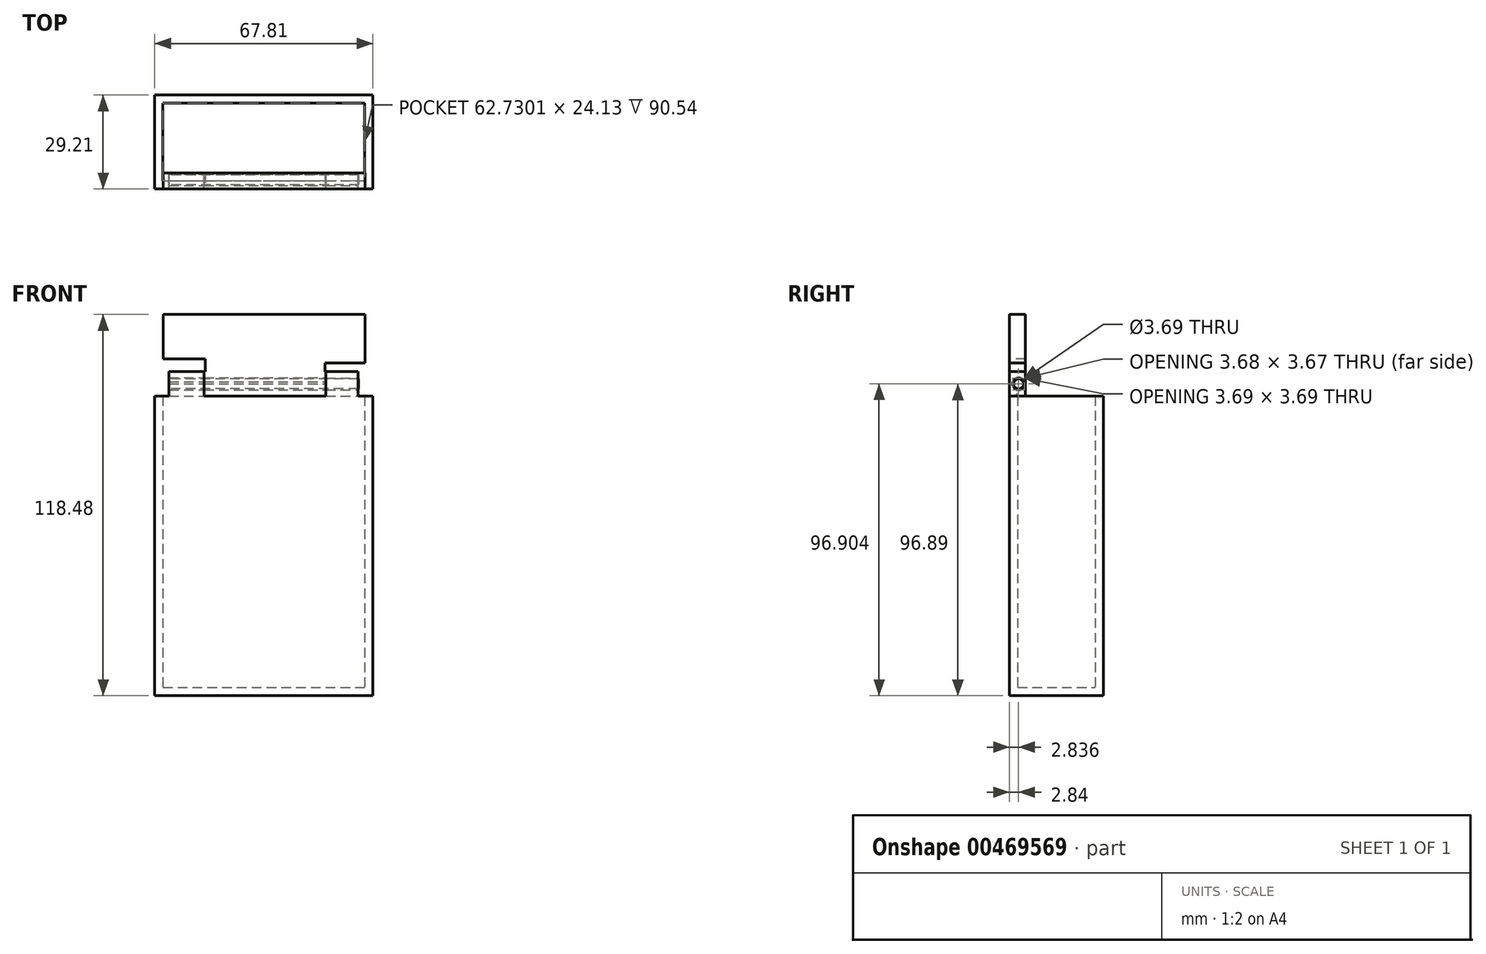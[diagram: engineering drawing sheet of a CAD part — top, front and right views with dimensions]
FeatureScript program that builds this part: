
annotation { "Feature Type Name" : "Feature", "Feature Type Description" : "" }
export const myFeature = defineFeature(function(context is Context, id is Id, definition is map)
    precondition{}
    {
        {
            var Q0;
            Q0=qCreatedBy(makeId("Top.planeOp"),FACE);
            var sketch = newSketch(context, id + "F0", { "sketchPlane" : qUnion([Q0])});
            skLineSegment(sketch, "E0.bottom", {"start": v(0, 0) * mm, "end": v(67.81, 0) * mm});
            skLineSegment(sketch, "E0.top", {"start": v(0, 29.21) * mm, "end": v(67.81, 29.21) * mm});
            skLineSegment(sketch, "E0.left", {"start": v(0, 0) * mm, "end": v(0, 29.21) * mm});
            skLineSegment(sketch, "E0.right", {"start": v(67.81, 0) * mm, "end": v(67.81, 29.21) * mm});
            skSolve(sketch);
        }
        {
            var Q0;
            Q0 = qSketchRegion(id + "F0", true);
            extrude(context, id + "F1", {"entities" : qUnion([Q0]), "depth" : 93.08 * mm});
        }
        {
            var Q0;
            Q0=makeQuery(id+"F1.opExtrude","CAP_FACE",FACE,{"disambiguationData":[OSD([sQuery(id+"F0.wireOp",EDGE,"E0.bottom"),sQuery(id+"F0.wireOp",EDGE,"E0.top"),sQuery(id+"F0.wireOp",EDGE,"E0.left"),sQuery(id+"F0.wireOp",EDGE,"E0.right")])],"isStart":false});
            shell(context, id + "F2", {"entities" : qUnion([Q0]), "thickness" : 2.54 * mm});
        }
        {
            var Q0;
            Q0=makeQuery(id+"F1.opExtrude","CAP_FACE",FACE,{"disambiguationData":[OSD([sQuery(id+"F0.wireOp",EDGE,"E0.bottom"),sQuery(id+"F0.wireOp",EDGE,"E0.top"),sQuery(id+"F0.wireOp",EDGE,"E0.left"),sQuery(id+"F0.wireOp",EDGE,"E0.right")])],"isStart":false});
            var sketch = newSketch(context, id + "F3", { "sketchPlane" : qUnion([Q0])});
            skLineSegment(sketch, "E1.bottom", {"start": v(4.45, 0) * mm, "end": v(15.39, 0) * mm});
            skLineSegment(sketch, "E1.top", {"start": v(4.45, 4.96) * mm, "end": v(15.39, 4.96) * mm});
            skLineSegment(sketch, "E1.left", {"start": v(4.45, 0) * mm, "end": v(4.45, 4.96) * mm});
            skLineSegment(sketch, "E1.right", {"start": v(15.39, 0) * mm, "end": v(15.39, 4.96) * mm});
            skLineSegment(sketch, "E2.bottom", {"start": v(63.22, 0) * mm, "end": v(53.2, 0) * mm});
            skLineSegment(sketch, "E2.top", {"start": v(63.22, 4.96) * mm, "end": v(53.2, 4.96) * mm});
            skLineSegment(sketch, "E2.left", {"start": v(63.22, 0) * mm, "end": v(63.22, 4.96) * mm});
            skLineSegment(sketch, "E2.right", {"start": v(53.2, 0) * mm, "end": v(53.2, 4.96) * mm});
            skSolve(sketch);
        }
        {
            var Q0;
            Q0 = qSketchRegion(id + "F3", true);
            extrude(context, id + "F4", {"entities" : qUnion([Q0]), "operationType" : NewBodyOperationType.ADD, "depth" : 7.62 * mm});
        }
        {
            var Q0;
            {var subQ2=sQuery(id+"F0.wireOp",EDGE,"E0.bottom");var subQ3=sQuery(id+"F3.wireOp",EDGE,"E1.right");Q0=makeQuery(id+"F4.boolean.opBoolean","SPLIT",FACE,{"disambiguationData":[TD([makeQuery(id+"F4.opExtrude","SWEPT_FACE",FACE,{"disambiguationData":[OSD([subQ3])]})])],"derivedFrom":makeQuery(id+"F1.opExtrude","CAP_FACE",FACE,{"disambiguationData":[OSD([subQ2,sQuery(id+"F0.wireOp",EDGE,"E0.top"),sQuery(id+"F0.wireOp",EDGE,"E0.left"),sQuery(id+"F0.wireOp",EDGE,"E0.right")])],"isStart":false})});}
            var sketch = newSketch(context, id + "F5", { "sketchPlane" : qUnion([Q0])});
            skLineSegment(sketch, "E3.bottom", {"start": v(15.39, 4.96) * mm, "end": v(53.2, 4.96) * mm});
            skLineSegment(sketch, "E3.top", {"start": v(15.39, 0) * mm, "end": v(53.2, 0) * mm});
            skLineSegment(sketch, "E3.left", {"start": v(15.39, 4.96) * mm, "end": v(15.39, 0) * mm});
            skLineSegment(sketch, "E3.right", {"start": v(53.2, 4.96) * mm, "end": v(53.2, 0) * mm});
            skSolve(sketch);
        }
        {
            var Q0;
            Q0 = qSketchRegion(id + "F5", true);
            extrude(context, id + "F6", {"entities" : qUnion([Q0]), "depth" : 25.4 * mm});
        }
        {
            var Q0;
            Q0=makeQuery(id+"F6.opExtrude","SWEPT_FACE",FACE,{"disambiguationData":[OSD([sQuery(id+"F5.wireOp",EDGE,"E3.left")])]});
            var sketch = newSketch(context, id + "F7", { "sketchPlane" : qUnion([Q0])});
            skLineSegment(sketch, "E4.bottom", {"start": v(-4.96, 100.75) * mm, "end": v(0, 100.75) * mm});
            skLineSegment(sketch, "E4.top", {"start": v(-4.96, 118.48) * mm, "end": v(0, 118.48) * mm});
            skLineSegment(sketch, "E4.left", {"start": v(-4.96, 100.75) * mm, "end": v(-4.96, 118.48) * mm});
            skLineSegment(sketch, "E4.right", {"start": v(0, 100.75) * mm, "end": v(0, 118.48) * mm});
            skSolve(sketch);
        }
        {
            var Q0;
            Q0 = qSketchRegion(id + "F7", true);
            extrude(context, id + "F8", {"entities" : qUnion([Q0]), "operationType" : NewBodyOperationType.ADD, "depth" : 12.7 * mm});
        }
        {
            var Q0;
            Q0=makeQuery(id+"F6.opExtrude","SWEPT_FACE",FACE,{"disambiguationData":[OSD([sQuery(id+"F5.wireOp",EDGE,"E3.right")])]});
            var sketch = newSketch(context, id + "F9", { "sketchPlane" : qUnion([Q0])});
            skLineSegment(sketch, "E5.bottom", {"start": v(4.96, 100.73) * mm, "end": v(0, 100.73) * mm});
            skLineSegment(sketch, "E5.top", {"start": v(4.96, 118.48) * mm, "end": v(0, 118.48) * mm});
            skLineSegment(sketch, "E5.left", {"start": v(4.96, 100.73) * mm, "end": v(4.96, 118.48) * mm});
            skLineSegment(sketch, "E5.right", {"start": v(0, 100.73) * mm, "end": v(0, 118.48) * mm});
            skSolve(sketch);
        }
        {
            var Q0;
            Q0 = qSketchRegion(id + "F9", true);
            extrude(context, id + "F10", {"entities" : qUnion([Q0]), "operationType" : NewBodyOperationType.ADD, "depth" : 12.2 * mm});
        }
        {
            var Q0;
            Q0=makeQuery(id+"F4.opExtrude","SWEPT_FACE",FACE,{"disambiguationData":[OSD([sQuery(id+"F3.wireOp",EDGE,"E2.left")])]});
            var sketch = newSketch(context, id + "F11", { "sketchPlane" : qUnion([Q0])});
            skCircle(sketch, "E6", {"center": v(2.84, 96.9) * mm, "radius": 1.84 * mm});
            skPoint(sketch, "E6.centerSnap0", {"position": v(0, 96.9) * mm});
            skSolve(sketch);
        }
        {
            var Q0;
            Q0 = qSketchRegion(id + "F11", true);
            extrude(context, id + "F12", {"entities" : qUnion([Q0]), "operationType" : NewBodyOperationType.REMOVE, "oppositeDirection" : true, "depth" : 64.26 * mm});
        }
        {
            var Q0;
            Q0=makeQuery(id+"F6.opExtrude","SWEPT_FACE",FACE,{"disambiguationData":[OSD([sQuery(id+"F5.wireOp",EDGE,"E3.right")])]});
            var sketch = newSketch(context, id + "F13", { "sketchPlane" : qUnion([Q0])});
            skCircle(sketch, "E7", {"center": v(2.83, 96.92) * mm, "radius": 1.84 * mm});
            skSolve(sketch);
        }
        {
            var Q0;
            Q0 = qSketchRegion(id + "F13", true);
            extrude(context, id + "F14", {"entities" : qUnion([Q0]), "operationType" : NewBodyOperationType.REMOVE, "oppositeDirection" : true, "depth" : 56.64 * mm});
        }
        {
            var Q0;
            Q0=makeQuery(id+"F4.opExtrude","SWEPT_FACE",FACE,{"disambiguationData":[OSD([sQuery(id+"F3.wireOp",EDGE,"E1.left")])]});
            var sketch = newSketch(context, id + "F15", { "sketchPlane" : qUnion([Q0])});
            skCircle(sketch, "E8", {"center": v(-2.84, 96.9) * mm, "radius": 1.53 * mm});
            skSolve(sketch);
        }
        {
            var Q0;
            Q0 = qSketchRegion(id + "F15", true);
            extrude(context, id + "F16", {"entities" : qUnion([Q0]), "oppositeDirection" : true, "depth" : 58.93 * mm});
        }
        {
            var Q0;
            Q0=makeQuery(id+"F6.opExtrude","CAP_EDGE",EDGE,{"disambiguationData":[OSD([sQuery(id+"F5.wireOp",EDGE,"E3.bottom")])],"isStart":true});
            fillet(context, id + "F17", {"entities" : qUnion([Q0]), "radius" : 5.08 * mm, "tangentPropagation" : true, "allowEdgeOverflow" : false});
        }
        {
            var Q0;
            Q0=makeQuery(id+"F8.opExtrude","CAP_FACE",FACE,{"disambiguationData":[OSD([sQuery(id+"F7.wireOp",EDGE,"E4.bottom"),sQuery(id+"F7.wireOp",EDGE,"E4.top"),sQuery(id+"F7.wireOp",EDGE,"E4.left"),sQuery(id+"F7.wireOp",EDGE,"E4.right")])],"isStart":false});
            var sketch = newSketch(context, id + "F18", { "sketchPlane" : qUnion([Q0])});
            skLineSegment(sketch, "E9.bottom", {"start": v(-4.96, 104.7) * mm, "end": v(0, 104.7) * mm});
            skLineSegment(sketch, "E9.top", {"start": v(-4.96, 100.75) * mm, "end": v(0, 100.75) * mm});
            skLineSegment(sketch, "E9.left", {"start": v(-4.96, 104.7) * mm, "end": v(-4.96, 100.75) * mm});
            skLineSegment(sketch, "E9.right", {"start": v(0, 104.7) * mm, "end": v(0, 100.75) * mm});
            skLineSegment(sketch, "E10.bottom", {"start": v(0, 104.7) * mm, "end": v(-4.96, 104.7) * mm});
            skLineSegment(sketch, "E10.top", {"start": v(0, 100.75) * mm, "end": v(-4.96, 100.75) * mm});
            skSolve(sketch);
        }
        {
            var Q0;
            Q0 = qSketchRegion(id + "F18", true);
            extrude(context, id + "F19", {"entities" : qUnion([Q0]), "operationType" : NewBodyOperationType.REMOVE, "oppositeDirection" : true, "depth" : 12.95 * mm});
        }
        {
            var Q0;
            Q0=makeQuery(id+"F10.opExtrude","CAP_FACE",FACE,{"disambiguationData":[OSD([sQuery(id+"F9.wireOp",EDGE,"E5.bottom"),sQuery(id+"F9.wireOp",EDGE,"E5.top"),sQuery(id+"F9.wireOp",EDGE,"E5.left"),sQuery(id+"F9.wireOp",EDGE,"E5.right")])],"isStart":false});
            var sketch = newSketch(context, id + "F20", { "sketchPlane" : qUnion([Q0])});
            skLineSegment(sketch, "E11.bottom", {"start": v(4.96, 100.73) * mm, "end": v(0, 100.73) * mm});
            skLineSegment(sketch, "E11.top", {"start": v(4.96, 103.4) * mm, "end": v(0, 103.4) * mm});
            skLineSegment(sketch, "E11.left", {"start": v(4.96, 100.73) * mm, "end": v(4.96, 103.4) * mm});
            skLineSegment(sketch, "E11.right", {"start": v(0, 100.73) * mm, "end": v(0, 103.4) * mm});
            skSolve(sketch);
        }
        {
            var Q0;
            Q0 = qSketchRegion(id + "F20", true);
            extrude(context, id + "F21", {"entities" : qUnion([Q0]), "operationType" : NewBodyOperationType.REMOVE, "oppositeDirection" : true, "depth" : 12.45 * mm});
        }
    });
